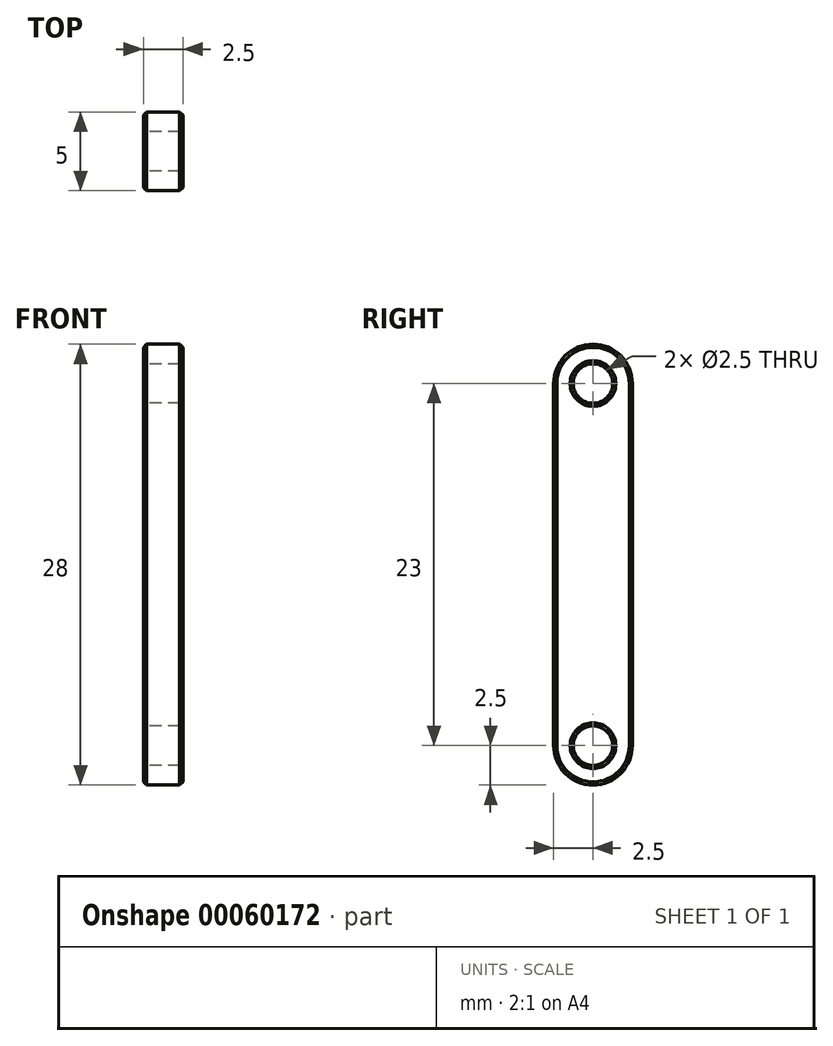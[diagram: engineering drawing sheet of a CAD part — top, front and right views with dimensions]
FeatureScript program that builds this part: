
annotation { "Feature Type Name" : "Feature", "Feature Type Description" : "" }
export const myFeature = defineFeature(function(context is Context, id is Id, definition is map)
    precondition{}
    {
        {
            var Q0;
            Q0=qCreatedBy(makeId("Right.planeOp"),FACE);
            var sketch = newSketch(context, id + "F0", { "sketchPlane" : qUnion([Q0])});
            skArc(sketch, "E0", {"start": v(2.5, 11.5) * mm, "mid": v(0, 14) * mm, "end": v(-2.5, 11.5) * mm});
            skArc(sketch, "E1", {"start": v(-2.5, -11.5) * mm, "mid": v(0, -14) * mm, "end": v(2.5, -11.5) * mm});
            skLineSegment(sketch, "E2", {"start": v(2.5, 11.5) * mm, "end": v(2.5, -11.5) * mm});
            skLineSegment(sketch, "E3", {"start": v(-2.5, 11.5) * mm, "end": v(-2.5, -11.5) * mm});
            skCircle(sketch, "E4", {"center": v(0, 11.5) * mm, "radius": 1.25 * mm});
            skCircle(sketch, "E5", {"center": v(0, -11.5) * mm, "radius": 1.25 * mm});
            skSolve(sketch);
        }
        {
            var Q0;
            Q0=qSketchRegion(id+"F0",true);
            extrude(context, id + "F1", {"entities" : qUnion([Q0]), "depth" : 2.5 * mm, "symmetric" : true});
        }
        {
            var Q0;
            Q0=makeQuery(id+"F1.opExtrude","CAP_EDGE",EDGE,{"disambiguationData":[OSD([sQuery(id+"F0.wireOp",EDGE,"E2")])],"isStart":false});
            var Q1;
            Q1=makeQuery(id+"F1.opExtrude","CAP_EDGE",EDGE,{"disambiguationData":[OSD([sQuery(id+"F0.wireOp",EDGE,"E0")])],"isStart":false});
            var Q2;
            Q2=makeQuery(id+"F1.opExtrude","CAP_EDGE",EDGE,{"disambiguationData":[OSD([sQuery(id+"F0.wireOp",EDGE,"E3")])],"isStart":false});
            var Q3;
            Q3=makeQuery(id+"F1.opExtrude","CAP_EDGE",EDGE,{"disambiguationData":[OSD([sQuery(id+"F0.wireOp",EDGE,"E1")])],"isStart":false});
            var Q4;
            Q4=makeQuery(id+"F1.opExtrude","CAP_EDGE",EDGE,{"disambiguationData":[OSD([sQuery(id+"F0.wireOp",EDGE,"E0")])],"isStart":true});
            var Q5;
            Q5=makeQuery(id+"F1.opExtrude","CAP_EDGE",EDGE,{"disambiguationData":[OSD([sQuery(id+"F0.wireOp",EDGE,"E2")])],"isStart":true});
            var Q6;
            Q6=makeQuery(id+"F1.opExtrude","CAP_EDGE",EDGE,{"disambiguationData":[OSD([sQuery(id+"F0.wireOp",EDGE,"E3")])],"isStart":true});
            var Q7;
            Q7=makeQuery(id+"F1.opExtrude","CAP_EDGE",EDGE,{"disambiguationData":[OSD([sQuery(id+"F0.wireOp",EDGE,"E1")])],"isStart":true});
            var Q8;
            Q8=makeQuery(id+"F1.opExtrude","CAP_EDGE",EDGE,{"disambiguationData":[OSD([sQuery(id+"F0.wireOp",EDGE,"E4")])],"isStart":true});
            var Q9;
            Q9=makeQuery(id+"F1.opExtrude","CAP_EDGE",EDGE,{"disambiguationData":[OSD([sQuery(id+"F0.wireOp",EDGE,"E5")])],"isStart":true});
            var Q10;
            Q10=makeQuery(id+"F1.opExtrude","CAP_EDGE",EDGE,{"disambiguationData":[OSD([sQuery(id+"F0.wireOp",EDGE,"E4")])],"isStart":false});
            var Q11;
            Q11=makeQuery(id+"F1.opExtrude","CAP_EDGE",EDGE,{"disambiguationData":[OSD([sQuery(id+"F0.wireOp",EDGE,"E5")])],"isStart":false});
            chamfer(context, id + "F2", {"entities" : qUnion([Q0, Q1, Q2, Q3, Q4, Q5, Q6, Q7, Q8, Q9, Q10, Q11]), "width" : 0.2 * mm, "tangentPropagation" : true});
        }
    });
